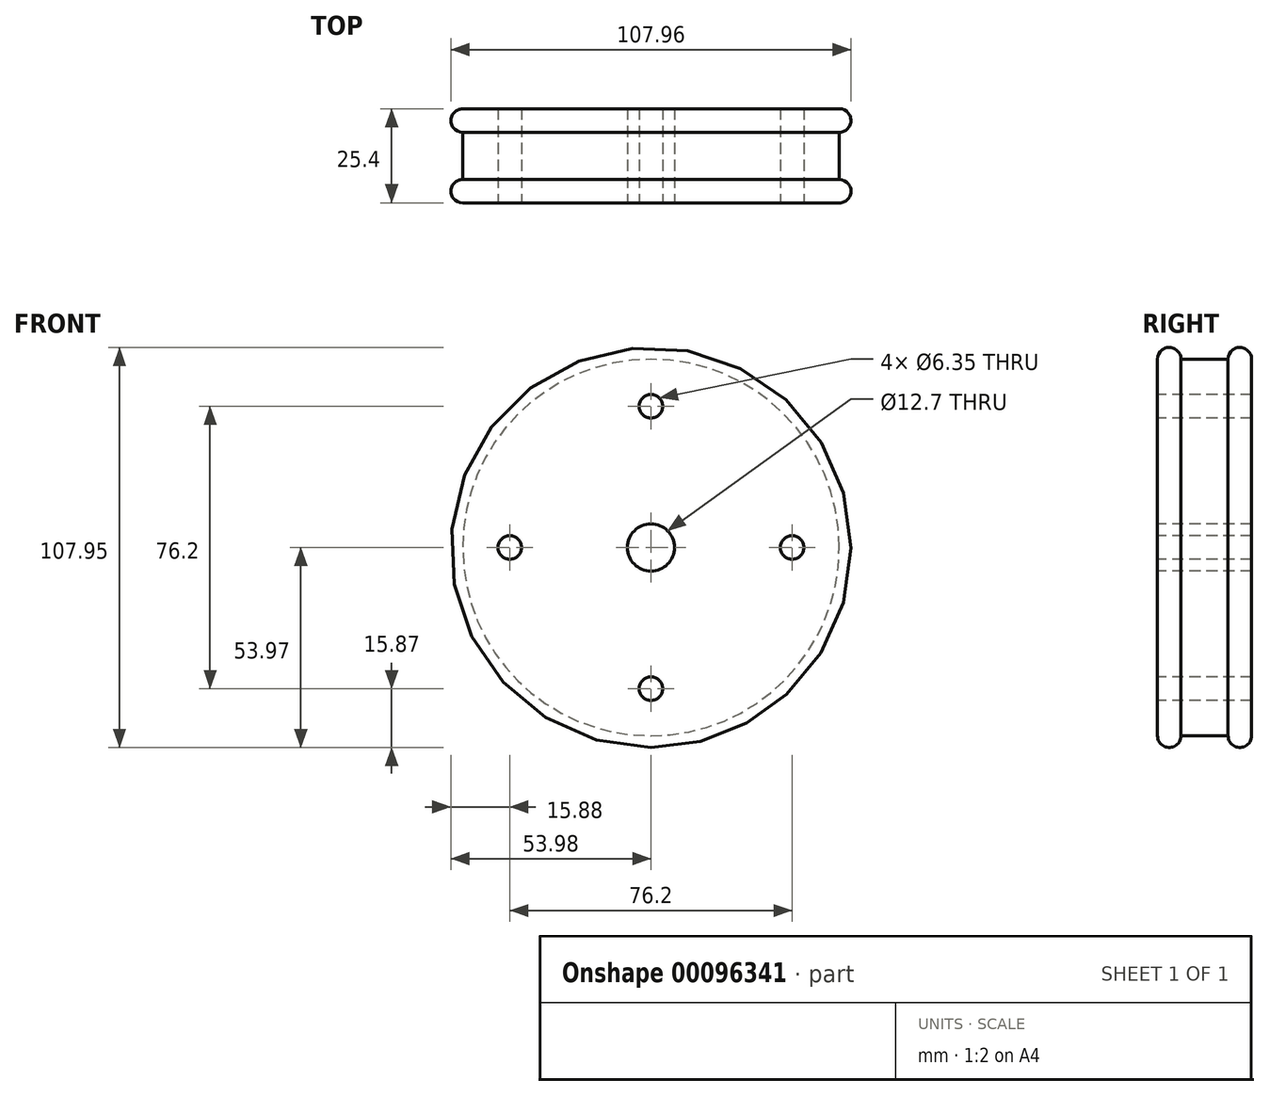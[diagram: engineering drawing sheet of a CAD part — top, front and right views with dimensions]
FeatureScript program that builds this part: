
annotation { "Feature Type Name" : "Feature", "Feature Type Description" : "" }
export const myFeature = defineFeature(function(context is Context, id is Id, definition is map)
    precondition{}
    {
        {
            var Q0;
            Q0=qCreatedBy(makeId("Front.planeOp"),FACE);
            var sketch = newSketch(context, id + "F0", { "sketchPlane" : qUnion([Q0])});
            skCircle(sketch, "E0", {"center": v(0, 0) * mm, "radius": 53.97 * mm});
            skSolve(sketch);
        }
        {
            var Q0;
            Q0 = qSketchRegion(id + "F0", true);
            extrude(context, id + "F1", {"entities" : qUnion([Q0]), "depth" : 6.35 * mm});
        }
        {
            var Q0;
            Q0=makeQuery(id+"F1.opExtrude","CAP_FACE",FACE,{"disambiguationData":[OSD([sQuery(id+"F0.wireOp",EDGE,"E0")])],"isStart":false});
            var sketch = newSketch(context, id + "F2", { "sketchPlane" : qUnion([Q0])});
            skCircle(sketch, "E1", {"center": v(0, 0) * mm, "radius": 50.8 * mm});
            skSolve(sketch);
        }
        {
            var Q0;
            Q0 = qSketchRegion(id + "F2", true);
            extrude(context, id + "F3", {"entities" : qUnion([Q0]), "operationType" : NewBodyOperationType.ADD, "depth" : 12.7 * mm});
        }
        {
            var Q0;
            Q0=makeQuery(id+"F3.opExtrude","CAP_FACE",FACE,{"disambiguationData":[OSD([sQuery(id+"F2.wireOp",EDGE,"E1")])],"isStart":false});
            var sketch = newSketch(context, id + "F4", { "sketchPlane" : qUnion([Q0])});
            skCircle(sketch, "E2", {"center": v(0, 0) * mm, "radius": 53.97 * mm});
            skSolve(sketch);
        }
        {
            var Q0;
            Q0 = qSketchRegion(id + "F4", true);
            extrude(context, id + "F5", {"entities" : qUnion([Q0]), "operationType" : NewBodyOperationType.ADD, "depth" : 6.35 * mm});
        }
        {
            var Q0;
            Q0=makeQuery(id+"F5.opExtrude","SWEPT_FACE",FACE,{"disambiguationData":[OSD([sQuery(id+"F4.wireOp",EDGE,"E2")])]});
            var Q1;
            Q1=makeQuery(id+"F1.opExtrude","SWEPT_FACE",FACE,{"disambiguationData":[OSD([sQuery(id+"F0.wireOp",EDGE,"E0")])]});
            fillet(context, id + "F6", {"entities" : qUnion([Q0, Q1]), "radius" : 3.17 * mm, "tangentPropagation" : true, "allowEdgeOverflow" : false});
        }
        {
            var Q0;
            Q0=makeQuery(id+"F5.opExtrude","CAP_FACE",FACE,{"disambiguationData":[OSD([sQuery(id+"F4.wireOp",EDGE,"E2")])],"isStart":false});
            var sketch = newSketch(context, id + "F7", { "sketchPlane" : qUnion([Q0])});
            skCircle(sketch, "E3", {"center": v(0, 0) * mm, "radius": 6.35 * mm});
            skCircle(sketch, "E4", {"center": v(0, 38.1) * mm, "radius": 3.18 * mm});
            skCircle(sketch, "E5", {"center": v(-38.1, 0) * mm, "radius": 3.18 * mm});
            skCircle(sketch, "E6", {"center": v(38.1, 0) * mm, "radius": 3.18 * mm});
            skCircle(sketch, "E7", {"center": v(0, -38.1) * mm, "radius": 3.18 * mm});
            skSolve(sketch);
        }
        {
            var Q0;
            Q0 = qSketchRegion(id + "F7", true);
            extrude(context, id + "F8", {"entities" : qUnion([Q0]), "operationType" : NewBodyOperationType.REMOVE, "endBound" : BoundingType.THROUGH_ALL, "oppositeDirection" : true, "depth" : 25.4 * mm});
        }
    });
